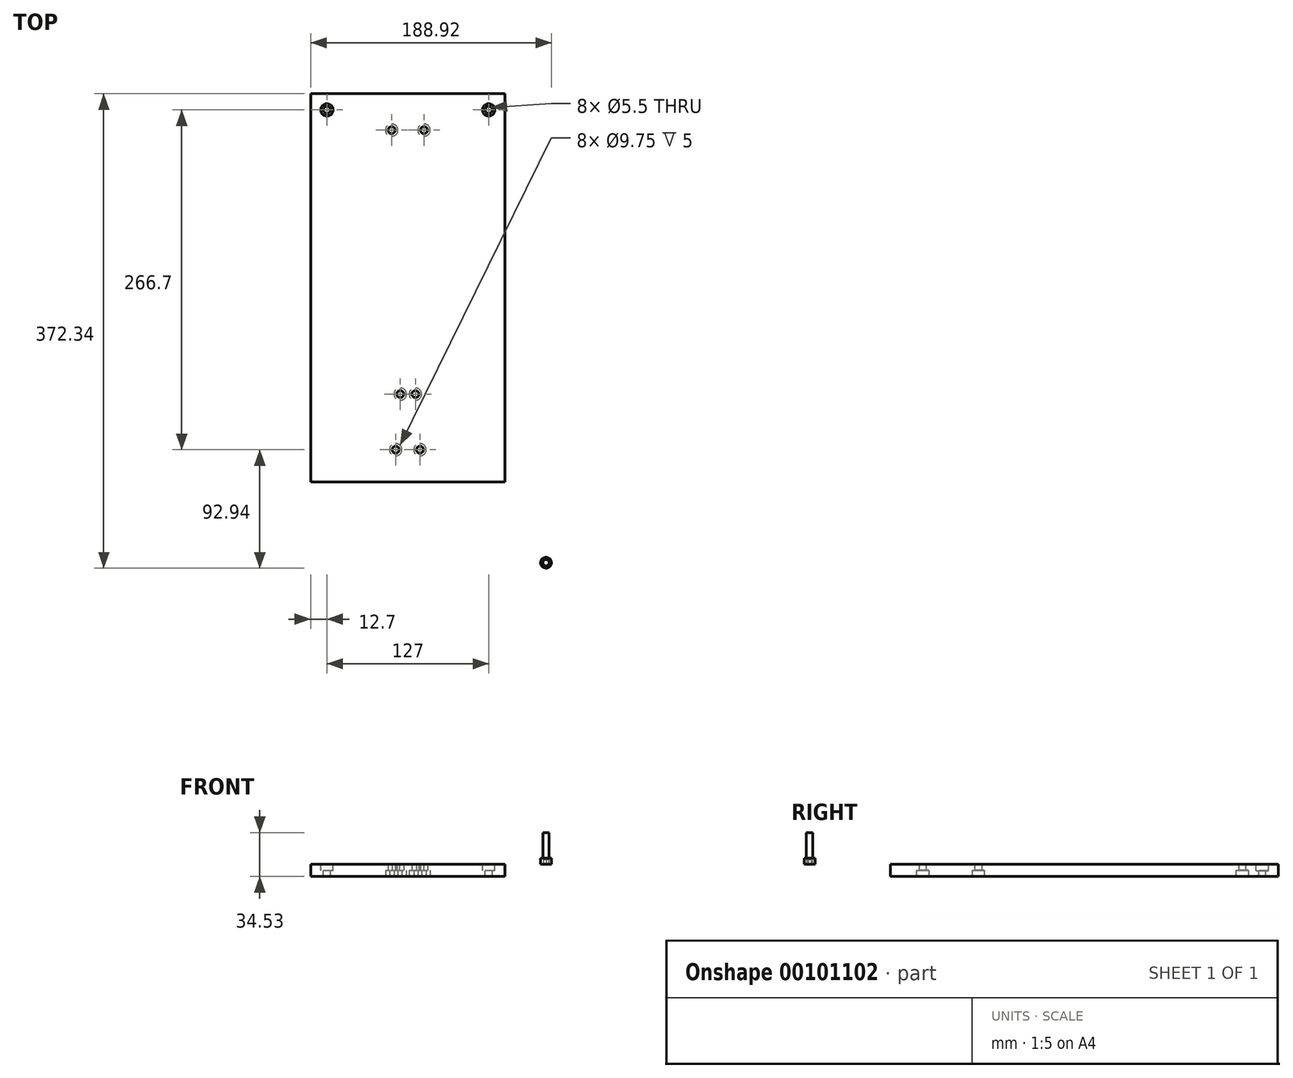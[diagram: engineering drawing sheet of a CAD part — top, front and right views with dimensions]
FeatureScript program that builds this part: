
annotation { "Feature Type Name" : "Feature", "Feature Type Description" : "" }
export const myFeature = defineFeature(function(context is Context, id is Id, definition is map)
    precondition{}
    {
        {
            var Q0;
            Q0=qCreatedBy(makeId("Top.planeOp"),FACE);
            var sketch = newSketch(context, id + "F0", { "sketchPlane" : qUnion([Q0])});
            skLineSegment(sketch, "E0.bottom", {"start": v(0, 0) * mm, "end": v(152.4, 0) * mm});
            skLineSegment(sketch, "E0.top", {"start": v(0, 317.5) * mm, "end": v(152.4, 317.5) * mm});
            skLineSegment(sketch, "E0.left", {"start": v(0, 0) * mm, "end": v(0, 317.5) * mm});
            skLineSegment(sketch, "E0.right", {"start": v(152.4, 0) * mm, "end": v(152.4, 317.5) * mm});
            skSolve(sketch);
        }
        {
            var Q0;
            Q0=makeQuery(id+"F0.imprint","IMPRINT",FACE,{"disambiguationData":[TD([[makeQuery(id+"F0.imprint","IMPRINT",EDGE,{"derivedFrom":sQuery(id+"F0.wireOp",EDGE,"E0.bottom")}),1.0]])]});
            extrude(context, id + "F1", {"entities" : qUnion([Q0]), "depth" : 9.52 * mm});
        }
        {
            var Q0;
            Q0=makeQuery(id+"F1.opExtrude","CAP_FACE",FACE,{"disambiguationData":[OSD([sQuery(id+"F0.wireOp",EDGE,"E0.bottom"),sQuery(id+"F0.wireOp",EDGE,"E0.top"),sQuery(id+"F0.wireOp",EDGE,"E0.left"),sQuery(id+"F0.wireOp",EDGE,"E0.right")])],"isStart":false});
            var sketch = newSketch(context, id + "F2", { "sketchPlane" : qUnion([Q0])});
            skLineSegment(sketch, "E1.bottom", {"start": v(76.2, 88.9) * mm, "end": v(64.3, 88.9) * mm});
            skLineSegment(sketch, "E1.top", {"start": v(76.2, 74.61) * mm, "end": v(64.3, 74.61) * mm});
            skLineSegment(sketch, "E1.left", {"start": v(76.2, 88.9) * mm, "end": v(76.2, 74.61) * mm, "construction": true});
            skLineSegment(sketch, "E1.right", {"start": v(64.3, 88.9) * mm, "end": v(64.3, 74.61) * mm});
            skLineSegment(sketch, "E2.MirrorCS", {"start": v(88.1, 88.9) * mm, "end": v(88.1, 74.61) * mm});
            skLineSegment(sketch, "E3.MirrorCS", {"start": v(76.2, 74.61) * mm, "end": v(88.1, 74.61) * mm});
            skLineSegment(sketch, "E4.MirrorCS", {"start": v(76.2, 88.9) * mm, "end": v(88.1, 88.9) * mm});
            skLineSegment(sketch, "E5", {"start": v(76.2, 0) * mm, "end": v(76.2, 25.4) * mm, "construction": true});
            skLineSegment(sketch, "E6.bottom", {"start": v(76.2, 25.4) * mm, "end": v(57.15, 25.4) * mm});
            skLineSegment(sketch, "E6.top", {"start": v(76.2, 50.8) * mm, "end": v(57.15, 50.8) * mm});
            skLineSegment(sketch, "E6.left", {"start": v(76.2, 25.4) * mm, "end": v(76.2, 50.8) * mm, "construction": true});
            skLineSegment(sketch, "E6.right", {"start": v(57.15, 25.4) * mm, "end": v(57.15, 50.8) * mm});
            skLineSegment(sketch, "E7.MirrorCS", {"start": v(76.2, 50.8) * mm, "end": v(95.25, 50.8) * mm});
            skLineSegment(sketch, "E8.MirrorCS", {"start": v(95.25, 25.4) * mm, "end": v(95.25, 50.8) * mm});
            skLineSegment(sketch, "E9.MirrorCS", {"start": v(76.2, 25.4) * mm, "end": v(95.25, 25.4) * mm});
            skLineSegment(sketch, "E10", {"start": v(76.2, 88.9) * mm, "end": v(76.2, 279.4) * mm, "construction": true});
            skLineSegment(sketch, "E11.bottom", {"start": v(76.2, 279.4) * mm, "end": v(50.8, 279.4) * mm});
            skLineSegment(sketch, "E11.top", {"start": v(76.2, 298.45) * mm, "end": v(50.8, 298.45) * mm});
            skLineSegment(sketch, "E11.left", {"start": v(76.2, 279.4) * mm, "end": v(76.2, 298.45) * mm, "construction": true});
            skLineSegment(sketch, "E11.right", {"start": v(50.8, 279.4) * mm, "end": v(50.8, 298.45) * mm});
            skLineSegment(sketch, "E12.MirrorCS", {"start": v(76.2, 298.45) * mm, "end": v(101.6, 298.45) * mm});
            skLineSegment(sketch, "E13.MirrorCS", {"start": v(101.6, 279.4) * mm, "end": v(101.6, 298.45) * mm});
            skLineSegment(sketch, "E14.MirrorCS", {"start": v(76.2, 279.4) * mm, "end": v(101.6, 279.4) * mm});
            skLineSegment(sketch, "E15", {"start": v(76.2, 279.4) * mm, "end": v(67.47, 279.4) * mm});
            skLineSegment(sketch, "E16", {"start": v(67.47, 279.4) * mm, "end": v(84.93, 279.4) * mm});
            skCircle(sketch, "E17", {"center": v(67.47, 279.4) * mm, "radius": 3.18 * mm});
            skCircle(sketch, "E18", {"center": v(84.93, 279.4) * mm, "radius": 3.18 * mm});
            skLineSegment(sketch, "E19.bottom", {"start": v(0, 317.5) * mm, "end": v(12.7, 317.5) * mm});
            skLineSegment(sketch, "E19.top", {"start": v(0, 304.8) * mm, "end": v(12.7, 304.8) * mm});
            skLineSegment(sketch, "E19.left", {"start": v(0, 317.5) * mm, "end": v(0, 304.8) * mm});
            skLineSegment(sketch, "E19.right", {"start": v(12.7, 317.5) * mm, "end": v(12.7, 304.8) * mm});
            skLineSegment(sketch, "E20.MirrorCS", {"start": v(152.4, 304.8) * mm, "end": v(139.7, 304.8) * mm});
            skLineSegment(sketch, "E21.MirrorCS", {"start": v(139.7, 317.5) * mm, "end": v(139.7, 304.8) * mm});
            skCircle(sketch, "E22", {"center": v(66.68, 38.1) * mm, "radius": 2.5 * mm});
            skPoint(sketch, "E22.centerSnap0", {"position": v(66.68, 50.8) * mm});
            skPoint(sketch, "E22.centerSnap1", {"position": v(57.15, 38.1) * mm});
            skCircle(sketch, "E23", {"center": v(70.25, 81.76) * mm, "radius": 2.5 * mm});
            skPoint(sketch, "E23.centerSnap0", {"position": v(64.3, 81.76) * mm});
            skPoint(sketch, "E23.centerSnap1", {"position": v(70.25, 74.61) * mm});
            skCircle(sketch, "E24", {"center": v(63.5, 288.93) * mm, "radius": 2.5 * mm});
            skPoint(sketch, "E24.centerSnap0", {"position": v(50.8, 288.93) * mm});
            skPoint(sketch, "E24.centerSnap1", {"position": v(63.5, 298.45) * mm});
            skCircle(sketch, "E25.MirrorC", {"center": v(88.9, 288.93) * mm, "radius": 2.5 * mm});
            skCircle(sketch, "E26.MirrorC", {"center": v(82.15, 81.76) * mm, "radius": 2.5 * mm});
            skCircle(sketch, "E27.MirrorC", {"center": v(85.73, 38.1) * mm, "radius": 2.5 * mm});
            skSolve(sketch);
        }
        {
            var Q0;
            Q0=sQuery(id+"F2.wireOp",VERTEX,"E23.center");
            var Q1;
            Q1=sQuery(id+"F2.wireOp",VERTEX,"E26.MirrorC.center");
            var Q2;
            Q2=sQuery(id+"F2.wireOp",VERTEX,"E22.center");
            var Q3;
            Q3=sQuery(id+"F2.wireOp",VERTEX,"E27.MirrorC.center");
            var Q4;
            Q4=sQuery(id+"F2.wireOp",VERTEX,"E25.MirrorC.center");
            var Q5;
            Q5=sQuery(id+"F2.wireOp",VERTEX,"E24.center");
            var Q6;
            Q6=makeQuery(id+"F1.opExtrude","SWEPT_BODY",BODY,{"disambiguationData":[OSD([sQuery(id+"F0.wireOp",EDGE,"E0.bottom"),sQuery(id+"F0.wireOp",EDGE,"E0.top"),sQuery(id+"F0.wireOp",EDGE,"E0.left"),sQuery(id+"F0.wireOp",EDGE,"E0.right")])]});
            hole(context, id + "F3", {"style" : HoleStyle.C_BORE, "endStyle" : HoleEndStyle.THROUGH, "standardTappedOrClearance" : lookupTablePath({ "standard" : "ISO", "fit" : "Normal", "size" : "M5", "type" : "Clearance" }), "standardBlindInLast" : lookupTablePath({ "fit" : "Standard", "standard" : "ISO", "size" : "M5", "type" : "Clearance" }), "holeDiameter" : 5.5 * mm, "cBoreDiameter" : 9.75 * mm, "cBoreDepth" : 5 * mm, "locations" : qUnion([Q0, Q1, Q2, Q3, Q4, Q5]), "scope" : qUnion([Q6]), "isTappedThrough" : true});
        }
        {
            var Q0;
            Q0=makeQuery(id+"F1.opExtrude","SWEPT_FACE",FACE,{"disambiguationData":[OSD([sQuery(id+"F0.wireOp",EDGE,"E0.bottom")])]});
            extrude(context, id + "F4", {"entities" : qUnion([Q0]), "operationType" : NewBodyOperationType.REMOVE, "oppositeDirection" : true, "depth" : 12.7 * mm});
        }
        {
            var Q0;
            Q0=makeQuery(id+"F1.opExtrude","SWEPT_BODY",BODY,{"disambiguationData":[OSD([sQuery(id+"F0.wireOp",EDGE,"E0.bottom"),sQuery(id+"F0.wireOp",EDGE,"E0.top"),sQuery(id+"F0.wireOp",EDGE,"E0.left"),sQuery(id+"F0.wireOp",EDGE,"E0.right")])]});
            var Q1;
            Q1=makeQuery(id+"F1.opExtrude","CAP_EDGE",EDGE,{"disambiguationData":[OSD([sQuery(id+"F0.wireOp",EDGE,"E0.left")])],"isStart":true});
            transform(context, id + "F5", {"entities" : qUnion([Q0]), "transformType" : TransformType.ROTATION, "transformAxis" : qUnion([Q1]), "angle" : 180 * degree, "makeCopy" : false});
        }
        {
            var Q0;
            Q0=qCreatedBy(makeId("Top.planeOp"),FACE);
            var sketch = newSketch(context, id + "F6", { "sketchPlane" : qUnion([Q0])});
            skCircle(sketch, "E28", {"center": v(32.27, -50.6) * mm, "radius": 4.25 * mm});
            skSolve(sketch);
        }
        {
            var Q0;
            Q0=makeQuery(id+"F6.imprint","IMPRINT",FACE,{"disambiguationData":[TD([[makeQuery(id+"F6.imprint","IMPRINT",EDGE,{"derivedFrom":sQuery(id+"F6.wireOp",EDGE,"E28")}),1.0]])]});
            extrude(context, id + "F7", {"entities" : qUnion([Q0]), "depth" : 5 * mm});
        }
        {
            var Q0;
            Q0=makeQuery(id+"F7.opExtrude","CAP_FACE",FACE,{"disambiguationData":[OSD([sQuery(id+"F6.wireOp",EDGE,"E28")])],"isStart":false});
            var sketch = newSketch(context, id + "F8", { "sketchPlane" : qUnion([Q0])});
            skCircle(sketch, "E29", {"center": v(32.27, -50.6) * mm, "radius": 2.5 * mm});
            skSolve(sketch);
        }
        {
            var Q0;
            Q0=makeQuery(id+"F8.imprint","IMPRINT",FACE,{"disambiguationData":[TD([[makeQuery(id+"F8.imprint","IMPRINT",EDGE,{"derivedFrom":sQuery(id+"F8.wireOp",EDGE,"E29")}),1.0]])]});
            extrude(context, id + "F9", {"entities" : qUnion([Q0]), "operationType" : NewBodyOperationType.ADD, "depth" : 20 * mm});
        }
        {
            var Q0;
            Q0=makeQuery(id+"F7.opExtrude","CAP_FACE",FACE,{"disambiguationData":[OSD([sQuery(id+"F6.wireOp",EDGE,"E28")])],"isStart":true});
            var sketch = newSketch(context, id + "F10", { "sketchPlane" : qUnion([Q0])});
            skCircle(sketch, "E30", {"center": v(32.27, 50.6) * mm, "radius": 2 * mm, "construction": true});
            skLineSegment(sketch, "E31.0", {"start": v(34.27, 51.75) * mm, "end": v(34.27, 49.44) * mm});
            skLineSegment(sketch, "E31.1", {"start": v(34.27, 49.44) * mm, "end": v(32.27, 48.29) * mm});
            skLineSegment(sketch, "E31.2", {"start": v(32.27, 48.29) * mm, "end": v(30.27, 49.44) * mm});
            skLineSegment(sketch, "E31.3", {"start": v(30.27, 49.44) * mm, "end": v(30.27, 51.75) * mm});
            skLineSegment(sketch, "E31.4", {"start": v(30.27, 51.75) * mm, "end": v(32.27, 52.9) * mm});
            skLineSegment(sketch, "E31.5", {"start": v(32.27, 52.9) * mm, "end": v(34.27, 51.75) * mm});
            skPoint(sketch, "E31.0.midPoint", {"position": v(34.27, 50.6) * mm});
            skSolve(sketch);
        }
        {
            var Q0;
            Q0=makeQuery(id+"F10.imprint","IMPRINT",FACE,{"disambiguationData":[TD([[makeQuery(id+"F10.imprint","IMPRINT",EDGE,{"derivedFrom":sQuery(id+"F10.wireOp",EDGE,"E31.0")}),-1.0]])]});
            var Q1;
            Q1=sQuery(id+"F10.wireOp",EDGE,"E30");
            extrude(context, id + "F11", {"entities" : qUnion([Q0]), "operationType" : NewBodyOperationType.REMOVE, "surfaceEntities" : qUnion([Q1]), "oppositeDirection" : true, "depth" : 4 * mm});
        }
        {
            var Q0;
            Q0=makeQuery(id+"F1.opExtrude","CAP_FACE",FACE,{"disambiguationData":[OSD([sQuery(id+"F0.wireOp",EDGE,"E0.bottom"),sQuery(id+"F0.wireOp",EDGE,"E0.top"),sQuery(id+"F0.wireOp",EDGE,"E0.left"),sQuery(id+"F0.wireOp",EDGE,"E0.right")])],"isStart":true});
            var sketch = newSketch(context, id + "F12", { "sketchPlane" : qUnion([Q0])});
            skLineSegment(sketch, "E32.bottom", {"start": v(-152.4, 317.5) * mm, "end": v(-139.7, 317.5) * mm});
            skLineSegment(sketch, "E32.top", {"start": v(-152.4, 304.8) * mm, "end": v(-139.7, 304.8) * mm});
            skLineSegment(sketch, "E32.left", {"start": v(-152.4, 317.5) * mm, "end": v(-152.4, 304.8) * mm});
            skLineSegment(sketch, "E32.right", {"start": v(-139.7, 317.5) * mm, "end": v(-139.7, 304.8) * mm});
            skLineSegment(sketch, "E33.bottom", {"start": v(0, 317.5) * mm, "end": v(-12.7, 317.5) * mm});
            skLineSegment(sketch, "E33.top", {"start": v(0, 304.8) * mm, "end": v(-12.7, 304.8) * mm});
            skLineSegment(sketch, "E33.left", {"start": v(0, 317.5) * mm, "end": v(0, 304.8) * mm});
            skLineSegment(sketch, "E33.right", {"start": v(-12.7, 317.5) * mm, "end": v(-12.7, 304.8) * mm});
            skSolve(sketch);
        }
        {
            var Q0;
            Q0=sQuery(id+"F12.wireOp",VERTEX,"E32.right.end");
            var Q1;
            Q1=sQuery(id+"F12.wireOp",VERTEX,"E33.top.end");
            var Q2;
            Q2=makeQuery(id+"F1.opExtrude","SWEPT_BODY",BODY,{"disambiguationData":[OSD([sQuery(id+"F0.wireOp",EDGE,"E0.bottom"),sQuery(id+"F0.wireOp",EDGE,"E0.top"),sQuery(id+"F0.wireOp",EDGE,"E0.left"),sQuery(id+"F0.wireOp",EDGE,"E0.right")])]});
            hole(context, id + "F13", {"style" : HoleStyle.C_BORE, "endStyle" : HoleEndStyle.THROUGH, "standardTappedOrClearance" : lookupTablePath({ "standard" : "ISO", "fit" : "Normal", "size" : "M5", "type" : "Clearance" }), "standardBlindInLast" : lookupTablePath({ "fit" : "Standard", "standard" : "ISO", "size" : "M5", "type" : "Clearance" }), "holeDiameter" : 5.5 * mm, "cBoreDiameter" : 9.75 * mm, "cBoreDepth" : 5 * mm, "locations" : qUnion([Q0, Q1]), "scope" : qUnion([Q2]), "isTappedThrough" : true});
        }
    });
